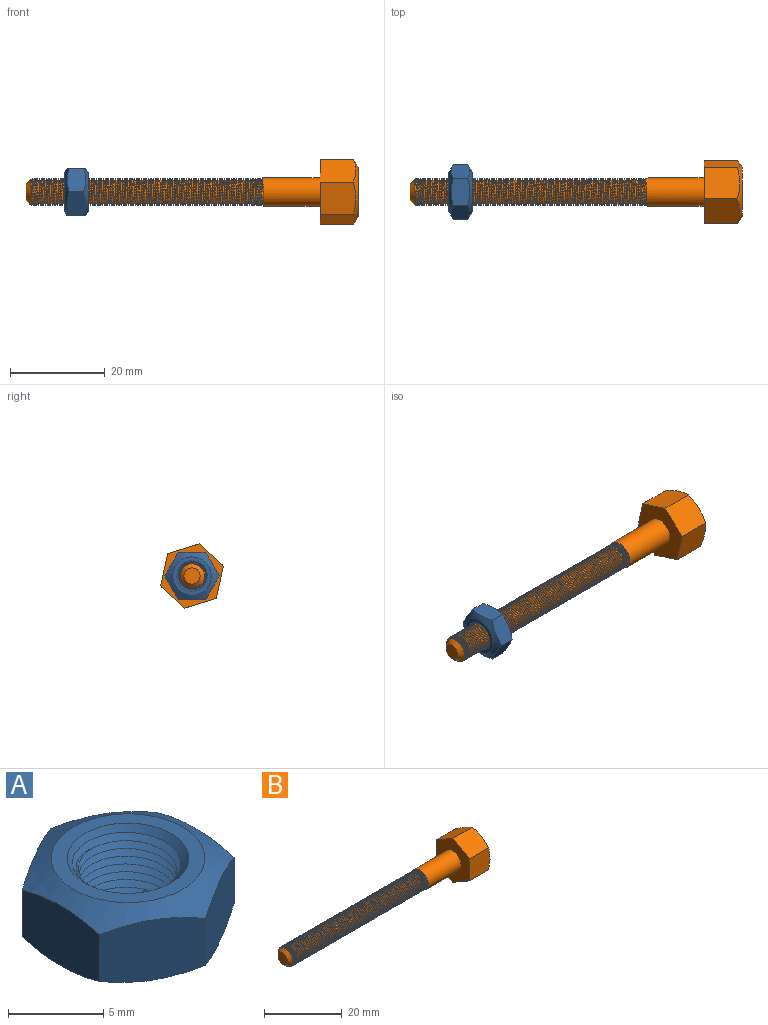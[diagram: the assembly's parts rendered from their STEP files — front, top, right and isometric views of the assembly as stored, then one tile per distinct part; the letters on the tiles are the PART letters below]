
ASSEMBLY  parts=2 mates=1
PART A: 15 faces, bbox 12x12x5.6 mm
  f0: plane 8.08x8.08mm, normal (0,0,-1), area 19.1mm2, adj f1,f11
  f1: cone r=5.77mm half-angle=60deg, axis (0,0,1), area 41.7mm2, adj f0,f2,f3,f4,f5,f6,f7
  f2: plane 5x3.9mm, normal (0.5,0.87,0), area 20.7mm2, adj f1,f3,f7,f8
  f3: plane 5x3.9mm, normal (-0.5,0.87,0), area 20.7mm2, adj f1,f2,f4,f8
  f4: plane 5.78x3.9mm, normal (-1,0,0), area 20.7mm2, adj f1,f3,f5,f8
  f5: plane 5x3.9mm, normal (-0.5,-0.87,0), area 20.7mm2, adj f1,f4,f6,f8
  f6: plane 5x3.9mm, normal (0.5,-0.87,0), area 20.7mm2, adj f1,f5,f7,f8
  f7: plane 6.25x4.37mm, normal (1,0,0), area 20.7mm2, adj f1,f2,f6,f8
  f8: cone r=5.77mm half-angle=60deg, axis (0,0,-1), area 40.7mm2, adj f2,f3,f4,f5,f6,f7,f9
  f9: plane 8.08x8.08mm, normal (0,0,1), area 19.1mm2, adj f8,f12
  f10: cone r=2.5mm half-angle=45deg, axis (0,0,-1), area 1.4mm2, adj f11,f13,f14
  f11: cone r=2.5mm half-angle=45deg, axis (0,0,-1), area 9.6mm2, adj f0,f10,f14
  f12: cone r=2.5mm half-angle=45deg, axis (0,0,1), area 11mm2, adj f9,f13,f14
  f13: bspline ~6.93x6mm, area 72.6mm2, adj f10,f12,f14
  f14: bspline ~6.93x6mm, area 73.8mm2, adj f10,f11,f12,f13
PART B: 32 faces, bbox 70.1x13.9x13.9 mm
  f0: plane 10.41x10.41mm, normal (1,0,0), area 71.1mm2, adj f18,f26,f27,f28,f29,f30,f31
  f1: cylinder r=3mm len=12.21mm, axis (-1,0,0), area 225.5mm2, adj f4,f7,f17
  f2: cone r=3mm half-angle=45deg, axis (1,0,0), area 19.1mm2, adj f3,f5,f6,f8
  f3: cone r=3mm half-angle=45deg, axis (1,0,0), area 0.7mm2, adj f2,f6,f10
  f4: plane 0.54x0.5mm, normal (0,0,-1), area 0.1mm2, adj f1,f5,f6,f7
  f5: bspline ~49.5x6.77mm, area 644.7mm2, adj f2,f4,f6,f9,f10
  f6: bspline ~49.5x6.77mm, area 649.3mm2, adj f2,f3,f4,f5,f7,f9,f10
  f7: bspline ~6.93x6mm, area 1.4mm2, adj f1,f4,f6
  f8: plane 3.4x3.4mm, normal (-1,0,0), area 9.1mm2, adj f2
  f9: plane 3.65x0.88mm, normal (-1,0,0), area 0.2mm2, adj f5,f6,f10
  f10: cylinder r=2.84mm len=48.48mm, axis (-1,0,0), area 303.7mm2, adj f3,f5,f6,f9
  f11: plane 7.54x6.93mm, normal (0,1,0), area 50.9mm2, adj f12,f16,f17,f18
  f12: plane 7.54x6mm, normal (0,0.5,0.87), area 50.9mm2, adj f11,f13,f17,f18
  f13: plane 7.54x6mm, normal (0,-0.5,0.87), area 50.9mm2, adj f12,f14,f17,f18
  f14: plane 7.54x6.93mm, normal (0,-1,0), area 50.9mm2, adj f13,f15,f17,f18
  f15: plane 7.54x6mm, normal (0,-0.5,-0.87), area 50.9mm2, adj f14,f16,f17,f18
  f16: plane 7.54x6mm, normal (0,0.5,-0.87), area 50.9mm2, adj f11,f15,f17,f18
  f17: plane 13.86x12mm, normal (-1,0,0), area 96.4mm2, adj f1,f11,f12,f13,f14,f15,f16
  f18: revolved ~13.86x13.86mm, area 45.9mm2, adj f0,f11,f12,f13,f14,f15,f16
  f19: plane 6.5x1.73mm, normal (0,-1,0), area 11.3mm2, adj f20,f24,f25,f29
  f20: plane 6.5x1.5mm, normal (0,-0.5,-0.87), area 11.3mm2, adj f19,f21,f25,f27
  f21: plane 6.5x1.5mm, normal (0,0.5,-0.87), area 11.3mm2, adj f20,f22,f25,f26
  f22: plane 6.5x1.73mm, normal (0,1,0), area 11.3mm2, adj f21,f23,f25,f28
  f23: plane 6.5x1.5mm, normal (0,0.5,0.87), area 11.3mm2, adj f22,f24,f25,f30
  f24: plane 6.5x1.5mm, normal (0,-0.5,0.87), area 11.3mm2, adj f19,f23,f25,f31
  f25: plane 3.46x3mm, normal (1,0,0), area 7.8mm2, adj f19,f20,f21,f22,f23,f24
  f26: plane 2x1.44mm, normal (0.71,0.35,-0.61), area 1.4mm2, adj f0,f21,f27,f28
  f27: plane 2x1.44mm, normal (0.71,-0.35,-0.61), area 1.4mm2, adj f0,f20,f26,f29
  f28: plane 2.31x0.5mm, normal (0.71,0.71,0), area 1.4mm2, adj f0,f22,f26,f30
  f29: plane 2.31x0.5mm, normal (0.71,-0.71,0), area 1.4mm2, adj f0,f19,f27,f31
  f30: plane 2x1.44mm, normal (0.71,0.35,0.61), area 1.4mm2, adj f0,f23,f28,f31
  f31: plane 2x1.44mm, normal (0.71,-0.35,0.61), area 1.4mm2, adj f0,f24,f29,f30
PLACE A rot(axis=(0,1,0),90deg) t=(20.39,-33.16,29.26)mm
PLACE B rot(axis=(1,0,0),12.4deg) t=(-3.16,-33.38,29.21)mm
MATE cylindrical A.f10 <-> B.f1  axis (1,0,0) through (25.39,-33.16,29.26)mm
